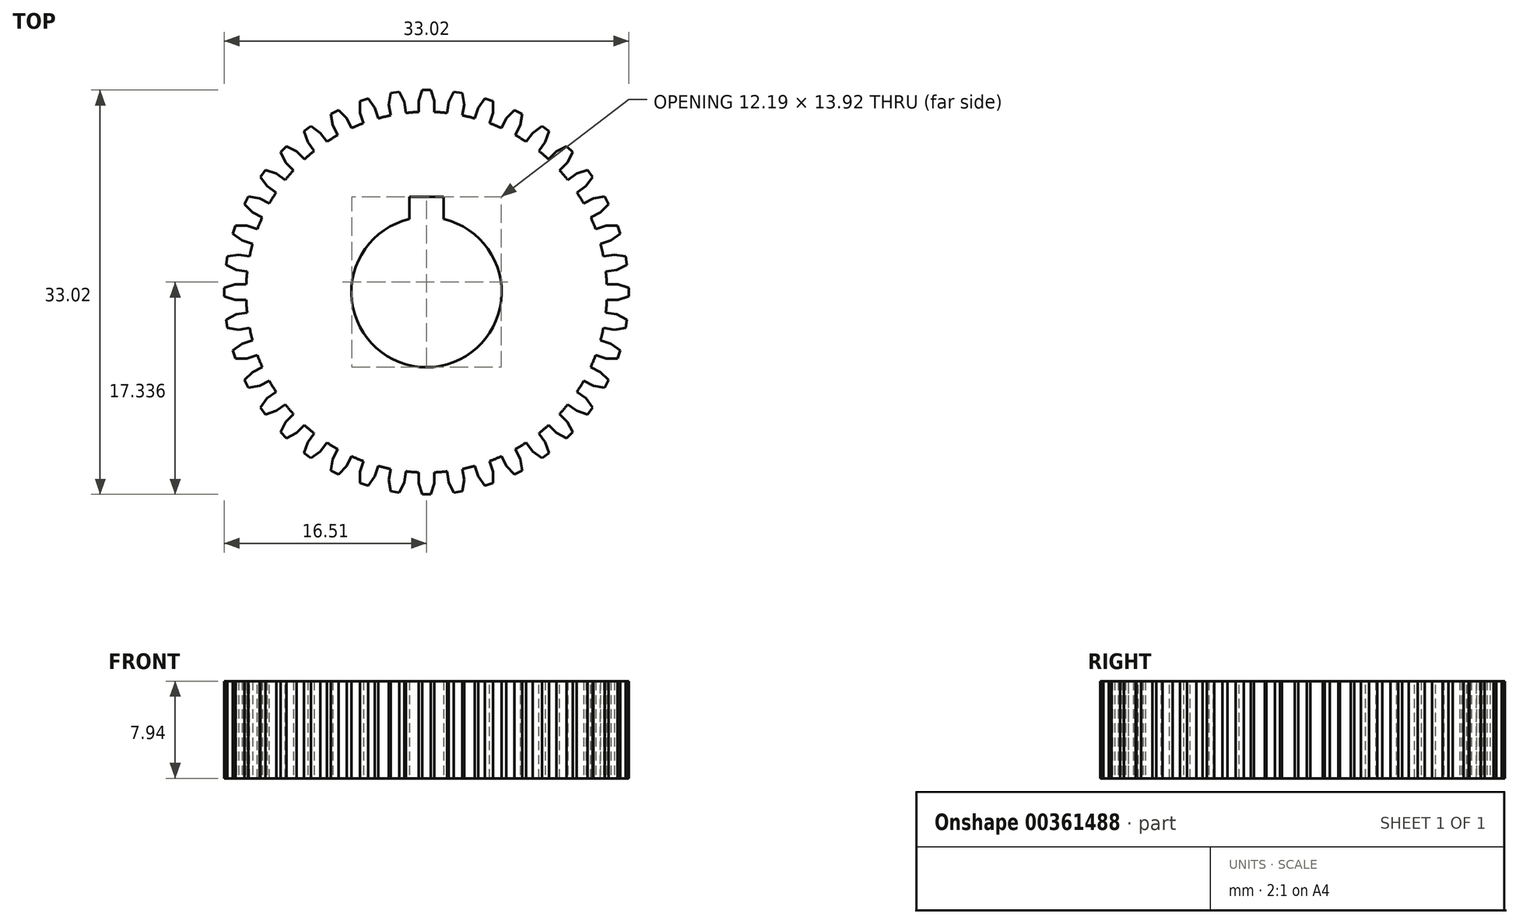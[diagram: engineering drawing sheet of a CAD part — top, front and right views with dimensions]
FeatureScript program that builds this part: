
annotation { "Feature Type Name" : "Feature", "Feature Type Description" : "" }
export const myFeature = defineFeature(function(context is Context, id is Id, definition is map)
    precondition{}
    {
        {
            var Q0;
            Q0=qCreatedBy(makeId("Top.planeOp"),FACE);
            var sketch = newSketch(context, id + "F0", { "sketchPlane" : qUnion([Q0])});
            skCircle(sketch, "E0", {"center": v(0, 0) * mm, "radius": 14.73 * mm});
            skLineSegment(sketch, "E1", {"start": v(-0.35, 16.51) * mm, "end": v(0.35, 16.51) * mm});
            skLineSegment(sketch, "E2", {"start": v(0.63, 14.72) * mm, "end": v(0.63, 15.61) * mm});
            skLineSegment(sketch, "E3", {"start": v(0.35, 16.51) * mm, "end": v(0.63, 15.61) * mm});
            skLineSegment(sketch, "E4.MirrorCS", {"start": v(-0.35, 16.51) * mm, "end": v(-0.63, 15.61) * mm});
            skLineSegment(sketch, "E5.MirrorCS", {"start": v(-0.63, 14.72) * mm, "end": v(-0.63, 15.61) * mm});
            skLineSegment(sketch, "E6.1.0", {"start": v(-2.93, 16.25) * mm, "end": v(-2.24, 16.36) * mm});
            skLineSegment(sketch, "E6.1.1", {"start": v(-1.68, 14.64) * mm, "end": v(-1.82, 15.52) * mm});
            skLineSegment(sketch, "E6.1.2", {"start": v(-2.24, 16.36) * mm, "end": v(-1.82, 15.52) * mm});
            skLineSegment(sketch, "E6.1.3", {"start": v(-2.93, 14.44) * mm, "end": v(-3.07, 15.32) * mm});
            skLineSegment(sketch, "E6.1.4", {"start": v(-2.93, 16.25) * mm, "end": v(-3.07, 15.32) * mm});
            skLineSegment(sketch, "E6.2.0", {"start": v(-5.44, 15.6) * mm, "end": v(-4.77, 15.81) * mm});
            skLineSegment(sketch, "E6.2.1", {"start": v(-3.94, 14.2) * mm, "end": v(-4.22, 15.05) * mm});
            skLineSegment(sketch, "E6.2.2", {"start": v(-4.77, 15.81) * mm, "end": v(-4.22, 15.05) * mm});
            skLineSegment(sketch, "E6.2.3", {"start": v(-5.15, 13.8) * mm, "end": v(-5.43, 14.65) * mm});
            skLineSegment(sketch, "E6.2.4", {"start": v(-5.44, 15.6) * mm, "end": v(-5.43, 14.65) * mm});
            skLineSegment(sketch, "E7.1.3.0", {"start": v(-7.8, 14.55) * mm, "end": v(-7.18, 14.87) * mm});
            skLineSegment(sketch, "E7.3.3.0", {"start": v(-6.12, 13.4) * mm, "end": v(-6.52, 14.2) * mm});
            skLineSegment(sketch, "E7.6.3.0", {"start": v(-7.18, 14.87) * mm, "end": v(-6.52, 14.2) * mm});
            skLineSegment(sketch, "E7.9.3.0", {"start": v(-7.25, 12.83) * mm, "end": v(-7.65, 13.62) * mm});
            skLineSegment(sketch, "E7.12.3.0", {"start": v(-7.8, 14.55) * mm, "end": v(-7.65, 13.62) * mm});
            skLineSegment(sketch, "E7.1.4.0", {"start": v(-9.99, 13.15) * mm, "end": v(-9.42, 13.56) * mm});
            skLineSegment(sketch, "E7.3.4.0", {"start": v(-8.14, 12.28) * mm, "end": v(-8.66, 13) * mm});
            skLineSegment(sketch, "E7.6.4.0", {"start": v(-9.42, 13.56) * mm, "end": v(-8.66, 13) * mm});
            skLineSegment(sketch, "E7.9.4.0", {"start": v(-9.16, 11.53) * mm, "end": v(-9.7, 12.26) * mm});
            skLineSegment(sketch, "E7.12.4.0", {"start": v(-9.99, 13.15) * mm, "end": v(-9.7, 12.26) * mm});
            skLineSegment(sketch, "E7.1.5.0", {"start": v(-11.92, 11.43) * mm, "end": v(-11.43, 11.92) * mm});
            skLineSegment(sketch, "E7.3.5.0", {"start": v(-9.96, 10.86) * mm, "end": v(-10.6, 11.49) * mm});
            skLineSegment(sketch, "E7.6.5.0", {"start": v(-11.43, 11.92) * mm, "end": v(-10.6, 11.49) * mm});
            skLineSegment(sketch, "E7.9.5.0", {"start": v(-10.86, 9.96) * mm, "end": v(-11.49, 10.6) * mm});
            skLineSegment(sketch, "E7.12.5.0", {"start": v(-11.92, 11.43) * mm, "end": v(-11.49, 10.6) * mm});
            skLineSegment(sketch, "E7.1.6.0", {"start": v(-13.56, 9.42) * mm, "end": v(-13.15, 9.99) * mm});
            skLineSegment(sketch, "E7.3.6.0", {"start": v(-11.53, 9.16) * mm, "end": v(-12.26, 9.7) * mm});
            skLineSegment(sketch, "E7.6.6.0", {"start": v(-13.15, 9.99) * mm, "end": v(-12.26, 9.7) * mm});
            skLineSegment(sketch, "E7.9.6.0", {"start": v(-12.28, 8.14) * mm, "end": v(-13, 8.66) * mm});
            skLineSegment(sketch, "E7.12.6.0", {"start": v(-13.56, 9.42) * mm, "end": v(-13, 8.66) * mm});
            skLineSegment(sketch, "E7.1.7.0", {"start": v(-14.87, 7.18) * mm, "end": v(-14.55, 7.8) * mm});
            skLineSegment(sketch, "E7.3.7.0", {"start": v(-12.83, 7.25) * mm, "end": v(-13.62, 7.65) * mm});
            skLineSegment(sketch, "E7.6.7.0", {"start": v(-14.55, 7.8) * mm, "end": v(-13.62, 7.65) * mm});
            skLineSegment(sketch, "E7.9.7.0", {"start": v(-13.4, 6.12) * mm, "end": v(-14.2, 6.52) * mm});
            skLineSegment(sketch, "E7.12.7.0", {"start": v(-14.87, 7.18) * mm, "end": v(-14.2, 6.52) * mm});
            skLineSegment(sketch, "E7.1.8.0", {"start": v(-15.81, 4.77) * mm, "end": v(-15.6, 5.44) * mm});
            skLineSegment(sketch, "E7.3.8.0", {"start": v(-13.8, 5.15) * mm, "end": v(-14.65, 5.43) * mm});
            skLineSegment(sketch, "E7.6.8.0", {"start": v(-15.6, 5.44) * mm, "end": v(-14.65, 5.43) * mm});
            skLineSegment(sketch, "E7.9.8.0", {"start": v(-14.2, 3.94) * mm, "end": v(-15.05, 4.22) * mm});
            skLineSegment(sketch, "E7.12.8.0", {"start": v(-15.81, 4.77) * mm, "end": v(-15.05, 4.22) * mm});
            skLineSegment(sketch, "E7.1.9.0", {"start": v(-16.36, 2.24) * mm, "end": v(-16.25, 2.93) * mm});
            skLineSegment(sketch, "E7.3.9.0", {"start": v(-14.44, 2.93) * mm, "end": v(-15.32, 3.07) * mm});
            skLineSegment(sketch, "E7.6.9.0", {"start": v(-16.25, 2.93) * mm, "end": v(-15.32, 3.07) * mm});
            skLineSegment(sketch, "E7.9.9.0", {"start": v(-14.64, 1.68) * mm, "end": v(-15.52, 1.82) * mm});
            skLineSegment(sketch, "E7.12.9.0", {"start": v(-16.36, 2.24) * mm, "end": v(-15.52, 1.82) * mm});
            skLineSegment(sketch, "E7.1.10.0", {"start": v(-16.51, -0.35) * mm, "end": v(-16.51, 0.35) * mm});
            skLineSegment(sketch, "E7.3.10.0", {"start": v(-14.72, 0.63) * mm, "end": v(-15.61, 0.63) * mm});
            skLineSegment(sketch, "E7.6.10.0", {"start": v(-16.51, 0.35) * mm, "end": v(-15.61, 0.63) * mm});
            skLineSegment(sketch, "E7.9.10.0", {"start": v(-14.72, -0.63) * mm, "end": v(-15.61, -0.63) * mm});
            skLineSegment(sketch, "E7.12.10.0", {"start": v(-16.51, -0.35) * mm, "end": v(-15.61, -0.63) * mm});
            skLineSegment(sketch, "E7.1.11.0", {"start": v(-16.25, -2.93) * mm, "end": v(-16.36, -2.24) * mm});
            skLineSegment(sketch, "E7.3.11.0", {"start": v(-14.64, -1.68) * mm, "end": v(-15.52, -1.82) * mm});
            skLineSegment(sketch, "E7.6.11.0", {"start": v(-16.36, -2.24) * mm, "end": v(-15.52, -1.82) * mm});
            skLineSegment(sketch, "E7.9.11.0", {"start": v(-14.44, -2.93) * mm, "end": v(-15.32, -3.07) * mm});
            skLineSegment(sketch, "E7.12.11.0", {"start": v(-16.25, -2.93) * mm, "end": v(-15.32, -3.07) * mm});
            skLineSegment(sketch, "E7.1.12.0", {"start": v(-15.6, -5.44) * mm, "end": v(-15.81, -4.77) * mm});
            skLineSegment(sketch, "E7.3.12.0", {"start": v(-14.2, -3.94) * mm, "end": v(-15.05, -4.22) * mm});
            skLineSegment(sketch, "E7.6.12.0", {"start": v(-15.81, -4.77) * mm, "end": v(-15.05, -4.22) * mm});
            skLineSegment(sketch, "E7.9.12.0", {"start": v(-13.8, -5.15) * mm, "end": v(-14.65, -5.43) * mm});
            skLineSegment(sketch, "E7.12.12.0", {"start": v(-15.6, -5.44) * mm, "end": v(-14.65, -5.43) * mm});
            skLineSegment(sketch, "E7.1.13.0", {"start": v(-14.55, -7.8) * mm, "end": v(-14.87, -7.18) * mm});
            skLineSegment(sketch, "E7.3.13.0", {"start": v(-13.4, -6.12) * mm, "end": v(-14.2, -6.52) * mm});
            skLineSegment(sketch, "E7.6.13.0", {"start": v(-14.87, -7.18) * mm, "end": v(-14.2, -6.52) * mm});
            skLineSegment(sketch, "E7.9.13.0", {"start": v(-12.83, -7.25) * mm, "end": v(-13.62, -7.65) * mm});
            skLineSegment(sketch, "E7.12.13.0", {"start": v(-14.55, -7.8) * mm, "end": v(-13.62, -7.65) * mm});
            skLineSegment(sketch, "E7.1.14.0", {"start": v(-13.15, -9.99) * mm, "end": v(-13.56, -9.42) * mm});
            skLineSegment(sketch, "E7.3.14.0", {"start": v(-12.28, -8.14) * mm, "end": v(-13, -8.66) * mm});
            skLineSegment(sketch, "E7.6.14.0", {"start": v(-13.56, -9.42) * mm, "end": v(-13, -8.66) * mm});
            skLineSegment(sketch, "E7.9.14.0", {"start": v(-11.53, -9.16) * mm, "end": v(-12.26, -9.7) * mm});
            skLineSegment(sketch, "E7.12.14.0", {"start": v(-13.15, -9.99) * mm, "end": v(-12.26, -9.7) * mm});
            skLineSegment(sketch, "E7.1.15.0", {"start": v(-11.43, -11.92) * mm, "end": v(-11.92, -11.43) * mm});
            skLineSegment(sketch, "E7.3.15.0", {"start": v(-10.86, -9.96) * mm, "end": v(-11.49, -10.6) * mm});
            skLineSegment(sketch, "E7.6.15.0", {"start": v(-11.92, -11.43) * mm, "end": v(-11.49, -10.6) * mm});
            skLineSegment(sketch, "E7.9.15.0", {"start": v(-9.96, -10.86) * mm, "end": v(-10.6, -11.49) * mm});
            skLineSegment(sketch, "E7.12.15.0", {"start": v(-11.43, -11.92) * mm, "end": v(-10.6, -11.49) * mm});
            skLineSegment(sketch, "E7.1.16.0", {"start": v(-9.42, -13.56) * mm, "end": v(-9.99, -13.15) * mm});
            skLineSegment(sketch, "E7.3.16.0", {"start": v(-9.16, -11.53) * mm, "end": v(-9.7, -12.26) * mm});
            skLineSegment(sketch, "E7.6.16.0", {"start": v(-9.99, -13.15) * mm, "end": v(-9.7, -12.26) * mm});
            skLineSegment(sketch, "E7.9.16.0", {"start": v(-8.14, -12.28) * mm, "end": v(-8.66, -13) * mm});
            skLineSegment(sketch, "E7.12.16.0", {"start": v(-9.42, -13.56) * mm, "end": v(-8.66, -13) * mm});
            skLineSegment(sketch, "E7.1.17.0", {"start": v(-7.18, -14.87) * mm, "end": v(-7.8, -14.55) * mm});
            skLineSegment(sketch, "E7.3.17.0", {"start": v(-7.25, -12.83) * mm, "end": v(-7.65, -13.62) * mm});
            skLineSegment(sketch, "E7.6.17.0", {"start": v(-7.8, -14.55) * mm, "end": v(-7.65, -13.62) * mm});
            skLineSegment(sketch, "E7.9.17.0", {"start": v(-6.12, -13.4) * mm, "end": v(-6.52, -14.2) * mm});
            skLineSegment(sketch, "E7.12.17.0", {"start": v(-7.18, -14.87) * mm, "end": v(-6.52, -14.2) * mm});
            skLineSegment(sketch, "E7.1.18.0", {"start": v(-4.77, -15.81) * mm, "end": v(-5.44, -15.6) * mm});
            skLineSegment(sketch, "E7.3.18.0", {"start": v(-5.15, -13.8) * mm, "end": v(-5.43, -14.65) * mm});
            skLineSegment(sketch, "E7.6.18.0", {"start": v(-5.44, -15.6) * mm, "end": v(-5.43, -14.65) * mm});
            skLineSegment(sketch, "E7.9.18.0", {"start": v(-3.94, -14.2) * mm, "end": v(-4.22, -15.05) * mm});
            skLineSegment(sketch, "E7.12.18.0", {"start": v(-4.77, -15.81) * mm, "end": v(-4.22, -15.05) * mm});
            skLineSegment(sketch, "E7.1.19.0", {"start": v(-2.24, -16.36) * mm, "end": v(-2.93, -16.25) * mm});
            skLineSegment(sketch, "E7.3.19.0", {"start": v(-2.93, -14.44) * mm, "end": v(-3.07, -15.32) * mm});
            skLineSegment(sketch, "E7.6.19.0", {"start": v(-2.93, -16.25) * mm, "end": v(-3.07, -15.32) * mm});
            skLineSegment(sketch, "E7.9.19.0", {"start": v(-1.68, -14.64) * mm, "end": v(-1.82, -15.52) * mm});
            skLineSegment(sketch, "E7.12.19.0", {"start": v(-2.24, -16.36) * mm, "end": v(-1.82, -15.52) * mm});
            skLineSegment(sketch, "E7.1.20.0", {"start": v(0.35, -16.51) * mm, "end": v(-0.35, -16.51) * mm});
            skLineSegment(sketch, "E7.3.20.0", {"start": v(-0.63, -14.72) * mm, "end": v(-0.63, -15.61) * mm});
            skLineSegment(sketch, "E7.6.20.0", {"start": v(-0.35, -16.51) * mm, "end": v(-0.63, -15.61) * mm});
            skLineSegment(sketch, "E7.9.20.0", {"start": v(0.63, -14.72) * mm, "end": v(0.63, -15.61) * mm});
            skLineSegment(sketch, "E7.12.20.0", {"start": v(0.35, -16.51) * mm, "end": v(0.63, -15.61) * mm});
            skLineSegment(sketch, "E7.1.21.0", {"start": v(2.93, -16.25) * mm, "end": v(2.24, -16.36) * mm});
            skLineSegment(sketch, "E7.3.21.0", {"start": v(1.68, -14.64) * mm, "end": v(1.82, -15.52) * mm});
            skLineSegment(sketch, "E7.6.21.0", {"start": v(2.24, -16.36) * mm, "end": v(1.82, -15.52) * mm});
            skLineSegment(sketch, "E7.9.21.0", {"start": v(2.93, -14.44) * mm, "end": v(3.07, -15.32) * mm});
            skLineSegment(sketch, "E7.12.21.0", {"start": v(2.93, -16.25) * mm, "end": v(3.07, -15.32) * mm});
            skLineSegment(sketch, "E7.1.22.0", {"start": v(5.44, -15.6) * mm, "end": v(4.77, -15.81) * mm});
            skLineSegment(sketch, "E7.3.22.0", {"start": v(3.94, -14.2) * mm, "end": v(4.22, -15.05) * mm});
            skLineSegment(sketch, "E7.6.22.0", {"start": v(4.77, -15.81) * mm, "end": v(4.22, -15.05) * mm});
            skLineSegment(sketch, "E7.9.22.0", {"start": v(5.15, -13.8) * mm, "end": v(5.43, -14.65) * mm});
            skLineSegment(sketch, "E7.12.22.0", {"start": v(5.44, -15.6) * mm, "end": v(5.43, -14.65) * mm});
            skLineSegment(sketch, "E7.1.23.0", {"start": v(7.8, -14.55) * mm, "end": v(7.18, -14.87) * mm});
            skLineSegment(sketch, "E7.3.23.0", {"start": v(6.12, -13.4) * mm, "end": v(6.52, -14.2) * mm});
            skLineSegment(sketch, "E7.6.23.0", {"start": v(7.18, -14.87) * mm, "end": v(6.52, -14.2) * mm});
            skLineSegment(sketch, "E7.9.23.0", {"start": v(7.25, -12.83) * mm, "end": v(7.65, -13.62) * mm});
            skLineSegment(sketch, "E7.12.23.0", {"start": v(7.8, -14.55) * mm, "end": v(7.65, -13.62) * mm});
            skLineSegment(sketch, "E7.1.24.0", {"start": v(9.99, -13.15) * mm, "end": v(9.42, -13.56) * mm});
            skLineSegment(sketch, "E7.3.24.0", {"start": v(8.14, -12.28) * mm, "end": v(8.66, -13) * mm});
            skLineSegment(sketch, "E7.6.24.0", {"start": v(9.42, -13.56) * mm, "end": v(8.66, -13) * mm});
            skLineSegment(sketch, "E7.9.24.0", {"start": v(9.16, -11.53) * mm, "end": v(9.7, -12.26) * mm});
            skLineSegment(sketch, "E7.12.24.0", {"start": v(9.99, -13.15) * mm, "end": v(9.7, -12.26) * mm});
            skLineSegment(sketch, "E7.1.25.0", {"start": v(11.92, -11.43) * mm, "end": v(11.43, -11.92) * mm});
            skLineSegment(sketch, "E7.3.25.0", {"start": v(9.96, -10.86) * mm, "end": v(10.6, -11.49) * mm});
            skLineSegment(sketch, "E7.6.25.0", {"start": v(11.43, -11.92) * mm, "end": v(10.6, -11.49) * mm});
            skLineSegment(sketch, "E7.9.25.0", {"start": v(10.86, -9.96) * mm, "end": v(11.49, -10.6) * mm});
            skLineSegment(sketch, "E7.12.25.0", {"start": v(11.92, -11.43) * mm, "end": v(11.49, -10.6) * mm});
            skLineSegment(sketch, "E7.1.26.0", {"start": v(13.56, -9.42) * mm, "end": v(13.15, -9.99) * mm});
            skLineSegment(sketch, "E7.3.26.0", {"start": v(11.53, -9.16) * mm, "end": v(12.26, -9.7) * mm});
            skLineSegment(sketch, "E7.6.26.0", {"start": v(13.15, -9.99) * mm, "end": v(12.26, -9.7) * mm});
            skLineSegment(sketch, "E7.9.26.0", {"start": v(12.28, -8.14) * mm, "end": v(13, -8.66) * mm});
            skLineSegment(sketch, "E7.12.26.0", {"start": v(13.56, -9.42) * mm, "end": v(13, -8.66) * mm});
            skLineSegment(sketch, "E7.1.27.0", {"start": v(14.87, -7.18) * mm, "end": v(14.55, -7.8) * mm});
            skLineSegment(sketch, "E7.3.27.0", {"start": v(12.83, -7.25) * mm, "end": v(13.62, -7.65) * mm});
            skLineSegment(sketch, "E7.6.27.0", {"start": v(14.55, -7.8) * mm, "end": v(13.62, -7.65) * mm});
            skLineSegment(sketch, "E7.9.27.0", {"start": v(13.4, -6.12) * mm, "end": v(14.2, -6.52) * mm});
            skLineSegment(sketch, "E7.12.27.0", {"start": v(14.87, -7.18) * mm, "end": v(14.2, -6.52) * mm});
            skLineSegment(sketch, "E7.1.28.0", {"start": v(15.81, -4.77) * mm, "end": v(15.6, -5.44) * mm});
            skLineSegment(sketch, "E7.3.28.0", {"start": v(13.8, -5.15) * mm, "end": v(14.65, -5.43) * mm});
            skLineSegment(sketch, "E7.6.28.0", {"start": v(15.6, -5.44) * mm, "end": v(14.65, -5.43) * mm});
            skLineSegment(sketch, "E7.9.28.0", {"start": v(14.2, -3.94) * mm, "end": v(15.05, -4.22) * mm});
            skLineSegment(sketch, "E7.12.28.0", {"start": v(15.81, -4.77) * mm, "end": v(15.05, -4.22) * mm});
            skLineSegment(sketch, "E7.1.29.0", {"start": v(16.36, -2.24) * mm, "end": v(16.25, -2.93) * mm});
            skLineSegment(sketch, "E7.3.29.0", {"start": v(14.44, -2.93) * mm, "end": v(15.32, -3.07) * mm});
            skLineSegment(sketch, "E7.6.29.0", {"start": v(16.25, -2.93) * mm, "end": v(15.32, -3.07) * mm});
            skLineSegment(sketch, "E7.9.29.0", {"start": v(14.64, -1.68) * mm, "end": v(15.52, -1.82) * mm});
            skLineSegment(sketch, "E7.12.29.0", {"start": v(16.36, -2.24) * mm, "end": v(15.52, -1.82) * mm});
            skLineSegment(sketch, "E7.1.30.0", {"start": v(16.51, 0.35) * mm, "end": v(16.51, -0.35) * mm});
            skLineSegment(sketch, "E7.3.30.0", {"start": v(14.72, -0.63) * mm, "end": v(15.61, -0.63) * mm});
            skLineSegment(sketch, "E7.6.30.0", {"start": v(16.51, -0.35) * mm, "end": v(15.61, -0.63) * mm});
            skLineSegment(sketch, "E7.9.30.0", {"start": v(14.72, 0.63) * mm, "end": v(15.61, 0.63) * mm});
            skLineSegment(sketch, "E7.12.30.0", {"start": v(16.51, 0.35) * mm, "end": v(15.61, 0.63) * mm});
            skLineSegment(sketch, "E7.1.31.0", {"start": v(16.25, 2.93) * mm, "end": v(16.36, 2.24) * mm});
            skLineSegment(sketch, "E7.3.31.0", {"start": v(14.64, 1.68) * mm, "end": v(15.52, 1.82) * mm});
            skLineSegment(sketch, "E7.6.31.0", {"start": v(16.36, 2.24) * mm, "end": v(15.52, 1.82) * mm});
            skLineSegment(sketch, "E7.9.31.0", {"start": v(14.44, 2.93) * mm, "end": v(15.32, 3.07) * mm});
            skLineSegment(sketch, "E7.12.31.0", {"start": v(16.25, 2.93) * mm, "end": v(15.32, 3.07) * mm});
            skLineSegment(sketch, "E7.1.32.0", {"start": v(15.6, 5.44) * mm, "end": v(15.81, 4.77) * mm});
            skLineSegment(sketch, "E7.3.32.0", {"start": v(14.2, 3.94) * mm, "end": v(15.05, 4.22) * mm});
            skLineSegment(sketch, "E7.6.32.0", {"start": v(15.81, 4.77) * mm, "end": v(15.05, 4.22) * mm});
            skLineSegment(sketch, "E7.9.32.0", {"start": v(13.8, 5.15) * mm, "end": v(14.65, 5.43) * mm});
            skLineSegment(sketch, "E7.12.32.0", {"start": v(15.6, 5.44) * mm, "end": v(14.65, 5.43) * mm});
            skLineSegment(sketch, "E7.1.33.0", {"start": v(14.55, 7.8) * mm, "end": v(14.87, 7.18) * mm});
            skLineSegment(sketch, "E7.3.33.0", {"start": v(13.4, 6.12) * mm, "end": v(14.2, 6.52) * mm});
            skLineSegment(sketch, "E7.6.33.0", {"start": v(14.87, 7.18) * mm, "end": v(14.2, 6.52) * mm});
            skLineSegment(sketch, "E7.9.33.0", {"start": v(12.83, 7.25) * mm, "end": v(13.62, 7.65) * mm});
            skLineSegment(sketch, "E7.12.33.0", {"start": v(14.55, 7.8) * mm, "end": v(13.62, 7.65) * mm});
            skLineSegment(sketch, "E7.1.34.0", {"start": v(13.15, 9.99) * mm, "end": v(13.56, 9.42) * mm});
            skLineSegment(sketch, "E7.3.34.0", {"start": v(12.28, 8.14) * mm, "end": v(13, 8.66) * mm});
            skLineSegment(sketch, "E7.6.34.0", {"start": v(13.56, 9.42) * mm, "end": v(13, 8.66) * mm});
            skLineSegment(sketch, "E7.9.34.0", {"start": v(11.53, 9.16) * mm, "end": v(12.26, 9.7) * mm});
            skLineSegment(sketch, "E7.12.34.0", {"start": v(13.15, 9.99) * mm, "end": v(12.26, 9.7) * mm});
            skLineSegment(sketch, "E7.1.35.0", {"start": v(11.43, 11.92) * mm, "end": v(11.92, 11.43) * mm});
            skLineSegment(sketch, "E7.3.35.0", {"start": v(10.86, 9.96) * mm, "end": v(11.49, 10.6) * mm});
            skLineSegment(sketch, "E7.6.35.0", {"start": v(11.92, 11.43) * mm, "end": v(11.49, 10.6) * mm});
            skLineSegment(sketch, "E7.9.35.0", {"start": v(9.96, 10.86) * mm, "end": v(10.6, 11.49) * mm});
            skLineSegment(sketch, "E7.12.35.0", {"start": v(11.43, 11.92) * mm, "end": v(10.6, 11.49) * mm});
            skLineSegment(sketch, "E7.1.36.0", {"start": v(9.42, 13.56) * mm, "end": v(9.99, 13.15) * mm});
            skLineSegment(sketch, "E7.3.36.0", {"start": v(9.16, 11.53) * mm, "end": v(9.7, 12.26) * mm});
            skLineSegment(sketch, "E7.6.36.0", {"start": v(9.99, 13.15) * mm, "end": v(9.7, 12.26) * mm});
            skLineSegment(sketch, "E7.9.36.0", {"start": v(8.14, 12.28) * mm, "end": v(8.66, 13) * mm});
            skLineSegment(sketch, "E7.12.36.0", {"start": v(9.42, 13.56) * mm, "end": v(8.66, 13) * mm});
            skLineSegment(sketch, "E7.1.37.0", {"start": v(7.18, 14.87) * mm, "end": v(7.8, 14.55) * mm});
            skLineSegment(sketch, "E7.3.37.0", {"start": v(7.25, 12.83) * mm, "end": v(7.65, 13.62) * mm});
            skLineSegment(sketch, "E7.6.37.0", {"start": v(7.8, 14.55) * mm, "end": v(7.65, 13.62) * mm});
            skLineSegment(sketch, "E7.9.37.0", {"start": v(6.12, 13.4) * mm, "end": v(6.52, 14.2) * mm});
            skLineSegment(sketch, "E7.12.37.0", {"start": v(7.18, 14.87) * mm, "end": v(6.52, 14.2) * mm});
            skLineSegment(sketch, "E7.1.38.0", {"start": v(4.77, 15.81) * mm, "end": v(5.44, 15.6) * mm});
            skLineSegment(sketch, "E7.3.38.0", {"start": v(5.15, 13.8) * mm, "end": v(5.43, 14.65) * mm});
            skLineSegment(sketch, "E7.6.38.0", {"start": v(5.44, 15.6) * mm, "end": v(5.43, 14.65) * mm});
            skLineSegment(sketch, "E7.9.38.0", {"start": v(3.94, 14.2) * mm, "end": v(4.22, 15.05) * mm});
            skLineSegment(sketch, "E7.12.38.0", {"start": v(4.77, 15.81) * mm, "end": v(4.22, 15.05) * mm});
            skLineSegment(sketch, "E7.1.39.0", {"start": v(2.24, 16.36) * mm, "end": v(2.93, 16.25) * mm});
            skLineSegment(sketch, "E7.3.39.0", {"start": v(2.93, 14.44) * mm, "end": v(3.07, 15.32) * mm});
            skLineSegment(sketch, "E7.6.39.0", {"start": v(2.93, 16.25) * mm, "end": v(3.07, 15.32) * mm});
            skLineSegment(sketch, "E7.9.39.0", {"start": v(1.68, 14.64) * mm, "end": v(1.82, 15.52) * mm});
            skLineSegment(sketch, "E7.12.39.0", {"start": v(2.24, 16.36) * mm, "end": v(1.82, 15.52) * mm});
            skCircle(sketch, "E8", {"center": v(0, 0) * mm, "radius": 6.13 * mm});
            skLineSegment(sketch, "E9", {"start": v(0, 7.79) * mm, "end": v(1.4, 7.79) * mm});
            skLineSegment(sketch, "E10", {"start": v(0, 7.79) * mm, "end": v(-1.4, 7.79) * mm});
            skLineSegment(sketch, "E11", {"start": v(-1.4, 7.79) * mm, "end": v(-1.4, 5.97) * mm});
            skLineSegment(sketch, "E12", {"start": v(1.4, 7.79) * mm, "end": v(1.4, 5.97) * mm});
            skSolve(sketch);
        }
        {
            var Q0;
            Q0=makeQuery(id+"F0.imprint","IMPRINT",FACE,{"disambiguationData":[TD([[makeQuery(id+"F0.imprint","IMPRINT",EDGE,{"derivedFrom":sQuery(id+"F0.wireOp",EDGE,"E7.1.9.0")}),-1.0]])]});
            var Q1;
            Q1=makeQuery(id+"F0.imprint","IMPRINT",FACE,{"disambiguationData":[TD([[makeQuery(id+"F0.imprint","IMPRINT",EDGE,{"derivedFrom":sQuery(id+"F0.wireOp",EDGE,"E7.1.3.0")}),-1.0]])]});
            var Q2;
            Q2=makeQuery(id+"F0.imprint","IMPRINT",FACE,{"disambiguationData":[TD([[makeQuery(id+"F0.imprint","IMPRINT",EDGE,{"derivedFrom":sQuery(id+"F0.wireOp",EDGE,"E7.1.14.0")}),-1.0]])]});
            var Q3;
            Q3=makeQuery(id+"F0.imprint","IMPRINT",FACE,{"disambiguationData":[TD([[makeQuery(id+"F0.imprint","IMPRINT",EDGE,{"derivedFrom":sQuery(id+"F0.wireOp",EDGE,"E7.1.39.0")}),-1.0]])]});
            var Q4;
            Q4=makeQuery(id+"F0.imprint","IMPRINT",FACE,{"disambiguationData":[TD([[makeQuery(id+"F0.imprint","IMPRINT",EDGE,{"derivedFrom":sQuery(id+"F0.wireOp",EDGE,"E1")}),-1.0]])]});
            var Q5;
            Q5=makeQuery(id+"F0.imprint","IMPRINT",FACE,{"disambiguationData":[TD([[makeQuery(id+"F0.imprint","IMPRINT",EDGE,{"derivedFrom":sQuery(id+"F0.wireOp",EDGE,"E6.1.0")}),-1.0]])]});
            var Q6;
            Q6=makeQuery(id+"F0.imprint","IMPRINT",FACE,{"disambiguationData":[TD([[makeQuery(id+"F0.imprint","IMPRINT",EDGE,{"derivedFrom":sQuery(id+"F0.wireOp",EDGE,"E6.2.0")}),-1.0]])]});
            var Q7;
            Q7=makeQuery(id+"F0.imprint","IMPRINT",FACE,{"disambiguationData":[TD([[makeQuery(id+"F0.imprint","IMPRINT",EDGE,{"derivedFrom":sQuery(id+"F0.wireOp",EDGE,"E7.1.36.0")}),-1.0]])]});
            var Q8;
            Q8=makeQuery(id+"F0.imprint","IMPRINT",FACE,{"disambiguationData":[TD([[makeQuery(id+"F0.imprint","IMPRINT",EDGE,{"derivedFrom":sQuery(id+"F0.wireOp",EDGE,"E7.1.37.0")}),-1.0]])]});
            var Q9;
            Q9=makeQuery(id+"F0.imprint","IMPRINT",FACE,{"disambiguationData":[TD([[makeQuery(id+"F0.imprint","IMPRINT",EDGE,{"derivedFrom":sQuery(id+"F0.wireOp",EDGE,"E7.1.38.0")}),-1.0]])]});
            var Q10;
            Q10=makeQuery(id+"F0.imprint","IMPRINT",FACE,{"disambiguationData":[TD([[makeQuery(id+"F0.imprint","IMPRINT",EDGE,{"derivedFrom":sQuery(id+"F0.wireOp",EDGE,"E7.1.35.0")}),-1.0]])]});
            var Q11;
            Q11=makeQuery(id+"F0.imprint","IMPRINT",FACE,{"disambiguationData":[TD([[makeQuery(id+"F0.imprint","IMPRINT",EDGE,{"derivedFrom":sQuery(id+"F0.wireOp",EDGE,"E7.1.12.0")}),-1.0]])]});
            var Q12;
            Q12=makeQuery(id+"F0.imprint","IMPRINT",FACE,{"disambiguationData":[TD([[makeQuery(id+"F0.imprint","IMPRINT",EDGE,{"derivedFrom":sQuery(id+"F0.wireOp",EDGE,"E7.1.28.0")}),-1.0]])]});
            var Q13;
            Q13=makeQuery(id+"F0.imprint","IMPRINT",FACE,{"disambiguationData":[TD([[makeQuery(id+"F0.imprint","IMPRINT",EDGE,{"derivedFrom":sQuery(id+"F0.wireOp",EDGE,"E7.1.32.0")}),-1.0]])]});
            var Q14;
            Q14=makeQuery(id+"F0.imprint","IMPRINT",FACE,{"disambiguationData":[TD([[makeQuery(id+"F0.imprint","IMPRINT",EDGE,{"derivedFrom":sQuery(id+"F0.wireOp",EDGE,"E7.1.33.0")}),-1.0]])]});
            var Q15;
            Q15=makeQuery(id+"F0.imprint","IMPRINT",FACE,{"disambiguationData":[TD([[makeQuery(id+"F0.imprint","IMPRINT",EDGE,{"derivedFrom":sQuery(id+"F0.wireOp",EDGE,"E7.1.31.0")}),-1.0]])]});
            var Q16;
            Q16=makeQuery(id+"F0.imprint","IMPRINT",FACE,{"disambiguationData":[TD([[makeQuery(id+"F0.imprint","IMPRINT",EDGE,{"derivedFrom":sQuery(id+"F0.wireOp",EDGE,"E7.1.6.0")}),-1.0]])]});
            var Q17;
            Q17=makeQuery(id+"F0.imprint","IMPRINT",FACE,{"disambiguationData":[TD([[makeQuery(id+"F0.imprint","IMPRINT",EDGE,{"derivedFrom":sQuery(id+"F0.wireOp",EDGE,"E7.1.4.0")}),-1.0]])]});
            var Q18;
            Q18=makeQuery(id+"F0.imprint","IMPRINT",FACE,{"disambiguationData":[TD([[makeQuery(id+"F0.imprint","IMPRINT",EDGE,{"derivedFrom":sQuery(id+"F0.wireOp",EDGE,"E7.1.29.0")}),-1.0]])]});
            var Q19;
            Q19=makeQuery(id+"F0.imprint","IMPRINT",FACE,{"disambiguationData":[TD([[makeQuery(id+"F0.imprint","IMPRINT",EDGE,{"derivedFrom":sQuery(id+"F0.wireOp",EDGE,"E7.1.5.0")}),-1.0]])]});
            var Q20;
            Q20=makeQuery(id+"F0.imprint","IMPRINT",FACE,{"disambiguationData":[TD([[makeQuery(id+"F0.imprint","IMPRINT",EDGE,{"derivedFrom":sQuery(id+"F0.wireOp",EDGE,"E7.1.13.0")}),-1.0]])]});
            var Q21;
            Q21=makeQuery(id+"F0.imprint","IMPRINT",FACE,{"disambiguationData":[TD([[makeQuery(id+"F0.imprint","IMPRINT",EDGE,{"derivedFrom":sQuery(id+"F0.wireOp",EDGE,"E7.1.26.0")}),-1.0]])]});
            var Q22;
            Q22=makeQuery(id+"F0.imprint","IMPRINT",FACE,{"disambiguationData":[TD([[makeQuery(id+"F0.imprint","IMPRINT",EDGE,{"derivedFrom":sQuery(id+"F0.wireOp",EDGE,"E7.1.10.0")}),-1.0]])]});
            var Q23;
            Q23=makeQuery(id+"F0.imprint","IMPRINT",FACE,{"disambiguationData":[TD([[makeQuery(id+"F0.imprint","IMPRINT",EDGE,{"derivedFrom":sQuery(id+"F0.wireOp",EDGE,"E7.1.11.0")}),-1.0]])]});
            var Q24;
            Q24=makeQuery(id+"F0.imprint","IMPRINT",FACE,{"disambiguationData":[TD([[makeQuery(id+"F0.imprint","IMPRINT",EDGE,{"derivedFrom":sQuery(id+"F0.wireOp",EDGE,"E7.1.27.0")}),-1.0]])]});
            var Q25;
            Q25=makeQuery(id+"F0.imprint","IMPRINT",FACE,{"disambiguationData":[TD([[makeQuery(id+"F0.imprint","IMPRINT",EDGE,{"derivedFrom":sQuery(id+"F0.wireOp",EDGE,"E7.1.25.0")}),-1.0]])]});
            var Q26;
            Q26=makeQuery(id+"F0.imprint","IMPRINT",FACE,{"disambiguationData":[TD([[makeQuery(id+"F0.imprint","IMPRINT",EDGE,{"derivedFrom":sQuery(id+"F0.wireOp",EDGE,"E7.1.8.0")}),-1.0]])]});
            var Q27;
            Q27=makeQuery(id+"F0.imprint","IMPRINT",FACE,{"disambiguationData":[TD([[makeQuery(id+"F0.imprint","IMPRINT",EDGE,{"derivedFrom":sQuery(id+"F0.wireOp",EDGE,"E7.1.24.0")}),-1.0]])]});
            var Q28;
            Q28=makeQuery(id+"F0.imprint","IMPRINT",FACE,{"disambiguationData":[TD([[makeQuery(id+"F0.imprint","IMPRINT",EDGE,{"derivedFrom":sQuery(id+"F0.wireOp",EDGE,"E7.1.7.0")}),-1.0]])]});
            var Q29;
            Q29=makeQuery(id+"F0.imprint","IMPRINT",FACE,{"disambiguationData":[TD([[makeQuery(id+"F0.imprint","IMPRINT",EDGE,{"derivedFrom":sQuery(id+"F0.wireOp",EDGE,"E7.1.23.0")}),-1.0]])]});
            var Q30;
            Q30=makeQuery(id+"F0.imprint","IMPRINT",FACE,{"disambiguationData":[TD([[makeQuery(id+"F0.imprint","IMPRINT",EDGE,{"derivedFrom":sQuery(id+"F0.wireOp",EDGE,"E7.1.22.0")}),-1.0]])]});
            var Q31;
            Q31=makeQuery(id+"F0.imprint","IMPRINT",FACE,{"disambiguationData":[TD([[makeQuery(id+"F0.imprint","IMPRINT",EDGE,{"derivedFrom":sQuery(id+"F0.wireOp",EDGE,"E7.1.17.0")}),-1.0]])]});
            var Q32;
            Q32=makeQuery(id+"F0.imprint","IMPRINT",FACE,{"disambiguationData":[TD([[makeQuery(id+"F0.imprint","IMPRINT",EDGE,{"derivedFrom":sQuery(id+"F0.wireOp",EDGE,"E7.1.18.0")}),-1.0]])]});
            var Q33;
            Q33=makeQuery(id+"F0.imprint","IMPRINT",FACE,{"disambiguationData":[TD([[makeQuery(id+"F0.imprint","IMPRINT",EDGE,{"derivedFrom":sQuery(id+"F0.wireOp",EDGE,"E7.1.16.0")}),-1.0]])]});
            var Q34;
            Q34=makeQuery(id+"F0.imprint","IMPRINT",FACE,{"disambiguationData":[TD([[makeQuery(id+"F0.imprint","IMPRINT",EDGE,{"derivedFrom":sQuery(id+"F0.wireOp",EDGE,"E7.1.21.0")}),-1.0]])]});
            var Q35;
            Q35=makeQuery(id+"F0.imprint","IMPRINT",FACE,{"disambiguationData":[TD([[makeQuery(id+"F0.imprint","IMPRINT",EDGE,{"derivedFrom":sQuery(id+"F0.wireOp",EDGE,"E7.1.20.0")}),-1.0]])]});
            var Q36;
            Q36=makeQuery(id+"F0.imprint","IMPRINT",FACE,{"disambiguationData":[TD([[makeQuery(id+"F0.imprint","IMPRINT",EDGE,{"derivedFrom":sQuery(id+"F0.wireOp",EDGE,"E7.1.19.0")}),-1.0]])]});
            var Q37;
            Q37=makeQuery(id+"F0.imprint","IMPRINT",FACE,{"disambiguationData":[TD([[makeQuery(id+"F0.imprint","IMPRINT",EDGE,{"derivedFrom":sQuery(id+"F0.wireOp",EDGE,"E9")}),1.0]])]});
            var Q38;
            Q38=makeQuery(id+"F0.imprint","IMPRINT",FACE,{"disambiguationData":[TD([[makeQuery(id+"F0.imprint","IMPRINT",EDGE,{"derivedFrom":sQuery(id+"F0.wireOp",EDGE,"E7.1.15.0")}),-1.0]])]});
            var Q39;
            Q39=makeQuery(id+"F0.imprint","IMPRINT",FACE,{"disambiguationData":[TD([[makeQuery(id+"F0.imprint","IMPRINT",EDGE,{"derivedFrom":sQuery(id+"F0.wireOp",EDGE,"E7.1.34.0")}),-1.0]])]});
            var Q40;
            Q40=makeQuery(id+"F0.imprint","IMPRINT",FACE,{"disambiguationData":[TD([[makeQuery(id+"F0.imprint","IMPRINT",EDGE,{"derivedFrom":sQuery(id+"F0.wireOp",EDGE,"E7.1.30.0")}),-1.0]])]});
            extrude(context, id + "F1", {"entities" : qUnion([Q0, Q1, Q2, Q3, Q4, Q5, Q6, Q7, Q8, Q9, Q10, Q11, Q12, Q13, Q14, Q15, Q16, Q17, Q18, Q19, Q20, Q21, Q22, Q23, Q24, Q25, Q26, Q27, Q28, Q29, Q30, Q31, Q32, Q33, Q34, Q35, Q36, Q37, Q38, Q39, Q40]), "depth" : 7.94 * mm});
        }
    });
